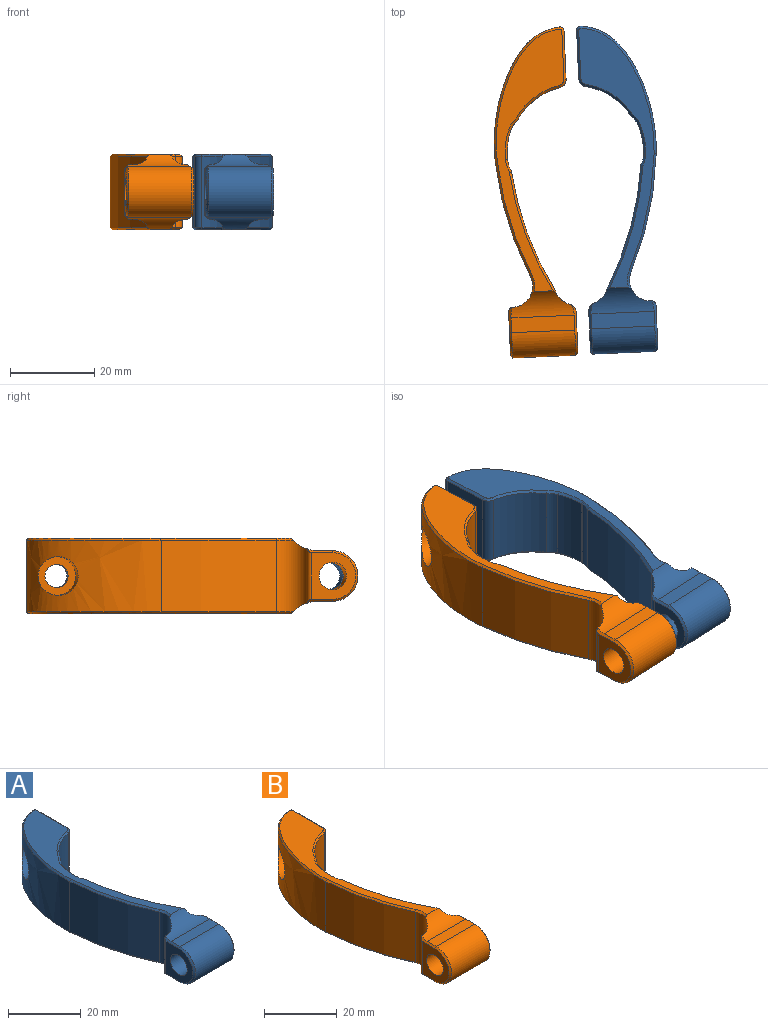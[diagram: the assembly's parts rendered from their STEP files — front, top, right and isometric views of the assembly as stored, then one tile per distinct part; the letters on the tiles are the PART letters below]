
ASSEMBLY  parts=2 mates=2
PART A: 63 faces, bbox 18.2x78.3x18.4 mm
  f0: cylinder r=74.99mm len=28.79mm, axis (0,0,-1), area 517.1mm2, adj f2,f25,f34,f47
  f1: plane 12.86x0.03mm, normal (0,1,0), area 0.4mm2, adj f3,f16,f18,f30
  f2: cylinder r=7.15mm len=17mm, axis (0,0,-1), area 3.1mm2, adj f0,f26,f32,f45
  f3: cylinder r=5mm len=17mm, axis (0,0,-1), area 158.4mm2, adj f1,f6,f16,f18,f31,f44
  f4: cylinder r=15.65mm len=17mm, axis (0,0,-1), area 225.5mm2, adj f24,f28,f43,f56
  f5: extruded ~31.05x17mm, area 568.3mm2, adj f6,f12,f29,f35,f48
  f6: cylinder r=78.49mm len=27.7mm, axis (0,0,-1), area 489.1mm2, adj f3,f5,f33,f46
  f7: plane 11x10.5mm, normal (-1,0,0), area 69.3mm2, adj f13,f30,f60,f61,f62
  f8: plane 62.05x16.98mm, normal (0,0,1), area 293.1mm2, adj f16,f44,f46,f47,f48,f49,f50,f51
  f9: plane 62.06x16.98mm, normal (0,0,-1), area 293.3mm2, adj f18,f31,f33,f34,f35,f36,f37,f38
  f10: cylinder r=2.75mm len=5.5mm, axis (1,0,0), area 34.6mm2, adj f11,f20
  f11: plane 9.2x9.2mm, normal (-1,0,0), area 42.7mm2, adj f10,f12
  f12: cylinder r=4.6mm len=12.12mm, axis (1,0,0), area 265.6mm2, adj f5,f11
  f13: cylinder r=3.25mm len=16mm, axis (-1,0,0), area 326.7mm2, adj f7,f19
  f14: plane 15x3.5mm, normal (0,0,1), area 52.5mm2, adj f15,f16,f57,f60
  f15: cylinder r=6mm len=15mm, axis (-1,0,0), area 282.7mm2, adj f14,f17,f58,f61
  f16: cylinder r=7.5mm len=15mm, axis (-1,0,0), area 71.3mm2, adj f1,f3,f8,f14,f21,f26,f27,f30
  f17: plane 15x3.5mm, normal (0,0,-1), area 52.5mm2, adj f15,f18,f59,f62
  f18: cylinder r=7.5mm len=15mm, axis (-1,0,0), area 71.3mm2, adj f1,f3,f9,f17,f21,f26,f27,f30
  f19: plane 11x9.66mm, normal (1,0,0), area 60.1mm2, adj f13,f27,f57,f58,f59
  f20: plane 17x11.43mm, normal (1,0,0), area 170.5mm2, adj f10,f28,f29,f39,f52
  f21: cylinder r=7.65mm len=13.29mm, axis (0,0,1), area 15.8mm2, adj f16,f18,f26,f27
  f22: cylinder r=16.15mm len=17mm, axis (0,0,1), area 117.6mm2, adj f23,f24,f40,f53
  f23: cylinder r=75.49mm len=17mm, axis (0,0,1), area 6.3mm2, adj f22,f25,f38,f51
  f24: cylinder r=5mm len=17mm, axis (0,0,1), area 46mm2, adj f4,f22,f42,f55
  f25: cylinder r=5mm len=17mm, axis (0,0,1), area 39.6mm2, adj f0,f23,f36,f49
  f26: cylinder r=5mm len=17.17mm, axis (0,0,1), area 57.3mm2, adj f2,f16,f18,f21,f32,f45
  f27: cylinder r=2mm len=12.87mm, axis (0,0,1), area 28.9mm2, adj f16,f18,f19,f21,f57,f59
  f28: cylinder r=2mm len=17mm, axis (0,0,-1), area 46.6mm2, adj f4,f20,f41,f54
  f29: cylinder r=1mm len=17mm, axis (0,0,-1), area 28.7mm2, adj f5,f20,f37,f50
  f30: cylinder r=1mm len=12.86mm, axis (0,0,-1), area 18.4mm2, adj f1,f7,f16,f18,f60,f62
  f31: cone r=5.5mm half-angle=45deg, axis (0,0,-1), area 2.9mm2, adj f3,f9,f18,f33
  f32: cone r=7.65mm half-angle=45deg, axis (0,0,-1), area 0.2mm2, adj f2,f18,f26,f34
  f33: cone r=78.49mm half-angle=45deg, axis (0,0,1), area 20.3mm2, adj f6,f9,f31,f35
  f34: cone r=75.49mm half-angle=45deg, axis (0,0,-1), area 21.5mm2, adj f0,f9,f18,f32,f36
  f35: bspline ~31.05x16.76mm, area 26.8mm2, adj f5,f9,f33,f37
  f36: cone r=5.5mm half-angle=45deg, axis (0,0,-1), area 1.7mm2, adj f9,f25,f34,f38
  f37: cone r=0.5mm half-angle=45deg, axis (0,0,1), area 0.9mm2, adj f9,f29,f35,f39
  f38: cone r=75.99mm half-angle=45deg, axis (0,0,-1), area 0.3mm2, adj f9,f23,f36,f40
  f39: plane 11.43x0.5mm, normal (0.71,0,-0.71), area 8.1mm2, adj f9,f20,f37,f41
  f40: cone r=16.65mm half-angle=45deg, axis (0,0,-1), area 5mm2, adj f9,f22,f38,f42
  f41: cone r=1.5mm half-angle=45deg, axis (0,0,1), area 1.7mm2, adj f9,f28,f39,f43
  f42: cone r=5.5mm half-angle=45deg, axis (0,0,-1), area 2mm2, adj f9,f24,f40,f43
  f43: cone r=16.15mm half-angle=45deg, axis (0,0,-1), area 9.5mm2, adj f4,f9,f41,f42
  f44: cone r=5.5mm half-angle=45deg, axis (0,0,1), area 2.9mm2, adj f3,f8,f16,f46
  f45: cone r=7.15mm half-angle=45deg, axis (0,0,1), area 0.2mm2, adj f2,f16,f26,f47
  f46: cone r=77.99mm half-angle=45deg, axis (0,0,-1), area 20.3mm2, adj f6,f8,f44,f48
  f47: cone r=74.99mm half-angle=45deg, axis (0,0,1), area 21.5mm2, adj f0,f8,f16,f45,f49
  f48: bspline ~31.05x16.76mm, area 26.8mm2, adj f5,f8,f46,f50
  f49: cone r=5.5mm half-angle=45deg, axis (0,0,1), area 1.7mm2, adj f8,f25,f47,f51
  f50: cone r=0.5mm half-angle=45deg, axis (0,0,-1), area 0.9mm2, adj f8,f29,f48,f52
  f51: cone r=75.49mm half-angle=45deg, axis (0,0,1), area 0.3mm2, adj f8,f23,f49,f53
  f52: plane 11.43x0.5mm, normal (0.71,0,0.71), area 8.1mm2, adj f8,f20,f50,f54
  f53: cone r=16.15mm half-angle=45deg, axis (0,0,1), area 5mm2, adj f8,f22,f51,f55
  f54: cone r=1.5mm half-angle=45deg, axis (0,0,-1), area 1.7mm2, adj f8,f28,f52,f56
  f55: cone r=5.5mm half-angle=45deg, axis (0,0,1), area 2mm2, adj f8,f24,f53,f56
  f56: cone r=15.65mm half-angle=45deg, axis (0,0,1), area 9.5mm2, adj f4,f8,f54,f55
  f57: plane 6.21x1.27mm, normal (0.71,0,0.71), area 3.9mm2, adj f14,f16,f19,f27,f58
  f58: cone r=5.5mm half-angle=45deg, axis (-1,0,0), area 12.8mm2, adj f15,f19,f57,f59
  f59: plane 6.21x1.27mm, normal (0.71,0,-0.71), area 3.9mm2, adj f17,f18,f19,f27,f58
  f60: plane 6x0.93mm, normal (-0.71,0,0.71), area 4.4mm2, adj f7,f14,f16,f30,f61
  f61: cone r=5.5mm half-angle=45deg, axis (1,0,0), area 12.8mm2, adj f7,f15,f60,f62
  f62: plane 6x0.93mm, normal (-0.71,0,-0.71), area 4.4mm2, adj f7,f17,f18,f30,f61
PART B: 68 faces, bbox 18.3x78.4x18.4 mm
  f0: cylinder r=75.04mm len=28.42mm, axis (0,0,-1), area 510.8mm2, adj f1,f31,f33,f48
  f1: cylinder r=7.2mm len=17mm, axis (0,0,-1), area 3.6mm2, adj f0,f25,f32,f47
  f2: cylinder r=5mm len=17mm, axis (0,0,-1), area 158.4mm2, adj f5,f15,f17,f29,f36,f49
  f3: cylinder r=15.7mm len=17mm, axis (0,0,-1), area 221mm2, adj f27,f30,f45,f61
  f4: extruded ~31.11x17mm, area 569.5mm2, adj f5,f11,f28,f40,f53
  f5: cylinder r=78.54mm len=27.75mm, axis (0,0,-1), area 490mm2, adj f2,f4,f38,f51
  f6: plane 11x10.5mm, normal (-1,0,0), area 69.3mm2, adj f12,f29,f65,f66,f67
  f7: plane 62.15x17.03mm, normal (0,0,1), area 293.6mm2, adj f15,f48,f49,f50,f51,f52,f53,f54
  f8: plane 62.16x17.03mm, normal (0,0,-1), area 293.8mm2, adj f17,f33,f34,f35,f36,f37,f38,f39
  f9: cylinder r=2.75mm len=5.5mm, axis (1,0,0), area 34.6mm2, adj f10,f19
  f10: plane 9.2x9.2mm, normal (-1,0,0), area 42.7mm2, adj f9,f11
  f11: cylinder r=4.6mm len=12.14mm, axis (1,0,0), area 265.9mm2, adj f4,f10
  f12: cylinder r=3.25mm len=16mm, axis (-1,0,0), area 326.7mm2, adj f6,f18
  f13: plane 15x3.5mm, normal (0,0,1), area 52.5mm2, adj f14,f15,f62,f65
  f14: cylinder r=6mm len=15mm, axis (-1,0,0), area 282.7mm2, adj f13,f16,f63,f66
  f15: cylinder r=7.5mm len=15mm, axis (-1,0,0), area 71.3mm2, adj f2,f7,f13,f20,f25,f26,f29,f47
  f16: plane 15x3.5mm, normal (0,0,-1), area 52.5mm2, adj f14,f17,f64,f67
  f17: cylinder r=7.5mm len=15mm, axis (-1,0,0), area 71.3mm2, adj f2,f8,f16,f20,f25,f26,f29,f32
  f18: plane 11x9.65mm, normal (1,0,0), area 60mm2, adj f12,f26,f62,f63,f64
  f19: plane 17x11.42mm, normal (1,0,0), area 170.5mm2, adj f9,f27,f28,f44,f57
  f20: cylinder r=7.7mm len=13.31mm, axis (0,0,1), area 16.4mm2, adj f15,f17,f25,f26
  f21: cylinder r=16.2mm len=17mm, axis (0,0,1), area 118.1mm2, adj f22,f23,f39,f56
  f22: cylinder r=75.54mm len=17mm, axis (0,0,1), area 6.3mm2, adj f21,f24,f37,f54
  f23: cylinder r=5mm len=17mm, axis (0,0,1), area 41.1mm2, adj f21,f30,f41,f58
  f24: cylinder r=5mm len=17mm, axis (0,0,1), area 33.9mm2, adj f22,f31,f35,f52
  f25: cylinder r=5mm len=17.17mm, axis (0,0,1), area 57mm2, adj f1,f15,f17,f20,f32,f47
  f26: cylinder r=2mm len=12.87mm, axis (0,0,1), area 28.9mm2, adj f15,f17,f18,f20,f62,f64
  f27: cylinder r=2mm len=17mm, axis (0,0,-1), area 46.6mm2, adj f3,f19,f46,f59
  f28: cylinder r=1mm len=17mm, axis (0,0,-1), area 28.7mm2, adj f4,f19,f42,f55
  f29: cylinder r=1mm len=12.86mm, axis (0,0,-1), area 18.4mm2, adj f2,f6,f15,f17,f65,f67
  f30: cylinder r=2mm len=17mm, axis (0,0,1), area 10.1mm2, adj f3,f23,f43,f60
  f31: cylinder r=2mm len=17mm, axis (0,0,1), area 12.3mm2, adj f0,f24,f34,f50
  f32: cone r=7.7mm half-angle=45deg, axis (0,0,-1), area 0.2mm2, adj f1,f17,f25,f33
  f33: cone r=75.54mm half-angle=45deg, axis (0,0,-1), area 21.3mm2, adj f0,f8,f17,f32,f34
  f34: cone r=1.5mm half-angle=45deg, axis (0,0,1), area 0.4mm2, adj f8,f31,f33,f35
  f35: cone r=5.5mm half-angle=45deg, axis (0,0,-1), area 1.5mm2, adj f8,f24,f34,f37
  f36: cone r=5.5mm half-angle=45deg, axis (0,0,-1), area 2.9mm2, adj f2,f8,f17,f38
  f37: cone r=76.04mm half-angle=45deg, axis (0,0,-1), area 0.3mm2, adj f8,f22,f35,f39
  f38: cone r=78.54mm half-angle=45deg, axis (0,0,1), area 20.3mm2, adj f5,f8,f36,f40
  f39: cone r=16.7mm half-angle=45deg, axis (0,0,-1), area 5mm2, adj f8,f21,f37,f41
  f40: bspline ~31.11x16.81mm, area 26.8mm2, adj f4,f8,f38,f42
  f41: cone r=5.5mm half-angle=45deg, axis (0,0,-1), area 1.8mm2, adj f8,f23,f39,f43
  f42: cone r=0.5mm half-angle=45deg, axis (0,0,1), area 0.9mm2, adj f8,f28,f40,f44
  f43: cone r=1.5mm half-angle=45deg, axis (0,0,1), area 0.4mm2, adj f8,f30,f41,f45
  f44: plane 11.42x0.5mm, normal (0.71,0,-0.71), area 8.1mm2, adj f8,f19,f42,f46
  f45: cone r=16.2mm half-angle=45deg, axis (0,0,-1), area 9.3mm2, adj f3,f8,f43,f46
  f46: cone r=1.5mm half-angle=45deg, axis (0,0,1), area 1.7mm2, adj f8,f27,f44,f45
  f47: cone r=7.2mm half-angle=45deg, axis (0,0,1), area 0.2mm2, adj f1,f15,f25,f48
  f48: cone r=75.04mm half-angle=45deg, axis (0,0,1), area 21.3mm2, adj f0,f7,f15,f47,f50
  f49: cone r=5.5mm half-angle=45deg, axis (0,0,1), area 2.9mm2, adj f2,f7,f15,f51
  f50: cone r=1.5mm half-angle=45deg, axis (0,0,-1), area 0.4mm2, adj f7,f31,f48,f52
  f51: cone r=78.04mm half-angle=45deg, axis (0,0,-1), area 20.3mm2, adj f5,f7,f49,f53
  f52: cone r=5.5mm half-angle=45deg, axis (0,0,1), area 1.5mm2, adj f7,f24,f50,f54
  f53: bspline ~31.11x16.81mm, area 26.8mm2, adj f4,f7,f51,f55
  f54: cone r=75.54mm half-angle=45deg, axis (0,0,1), area 0.3mm2, adj f7,f22,f52,f56
  f55: cone r=0.5mm half-angle=45deg, axis (0,0,-1), area 0.9mm2, adj f7,f28,f53,f57
  f56: cone r=16.2mm half-angle=45deg, axis (0,0,1), area 5mm2, adj f7,f21,f54,f58
  f57: plane 11.42x0.5mm, normal (0.71,0,0.71), area 8.1mm2, adj f7,f19,f55,f59
  f58: cone r=5.5mm half-angle=45deg, axis (0,0,1), area 1.8mm2, adj f7,f23,f56,f60
  f59: cone r=1.5mm half-angle=45deg, axis (0,0,-1), area 1.7mm2, adj f7,f27,f57,f61
  f60: cone r=1.5mm half-angle=45deg, axis (0,0,-1), area 0.4mm2, adj f7,f30,f58,f61
  f61: cone r=15.7mm half-angle=45deg, axis (0,0,1), area 9.3mm2, adj f3,f7,f59,f60
  f62: plane 6.2x1.26mm, normal (0.71,0,0.71), area 3.9mm2, adj f13,f15,f18,f26,f63
  f63: cone r=5.5mm half-angle=45deg, axis (-1,0,0), area 12.8mm2, adj f14,f18,f62,f64
  f64: plane 6.2x1.26mm, normal (0.71,0,-0.71), area 3.9mm2, adj f16,f17,f18,f26,f63
  f65: plane 6x0.93mm, normal (-0.71,0,0.71), area 4.4mm2, adj f6,f13,f15,f29,f66
  f66: cone r=5.5mm half-angle=45deg, axis (1,0,0), area 12.8mm2, adj f6,f14,f65,f67
  f67: plane 6x0.93mm, normal (-0.71,0,-0.71), area 4.4mm2, adj f6,f16,f17,f29,f66
PLACE A rot(axis=(-0.02,1,0),180deg) t=(12.7,18.95,11)mm
PLACE B rot(axis=(0,0,1),2.5deg) t=(12.7,18.9,-7)mm
MATE parallel B.f9 <-> A.f10  axis (1,0.04,0) through (10.22,41.61,2)mm
MATE cylindrical A.f10 <-> B.f9  axis (-1,-0.04,0) through (13.22,41.74,2)mm
